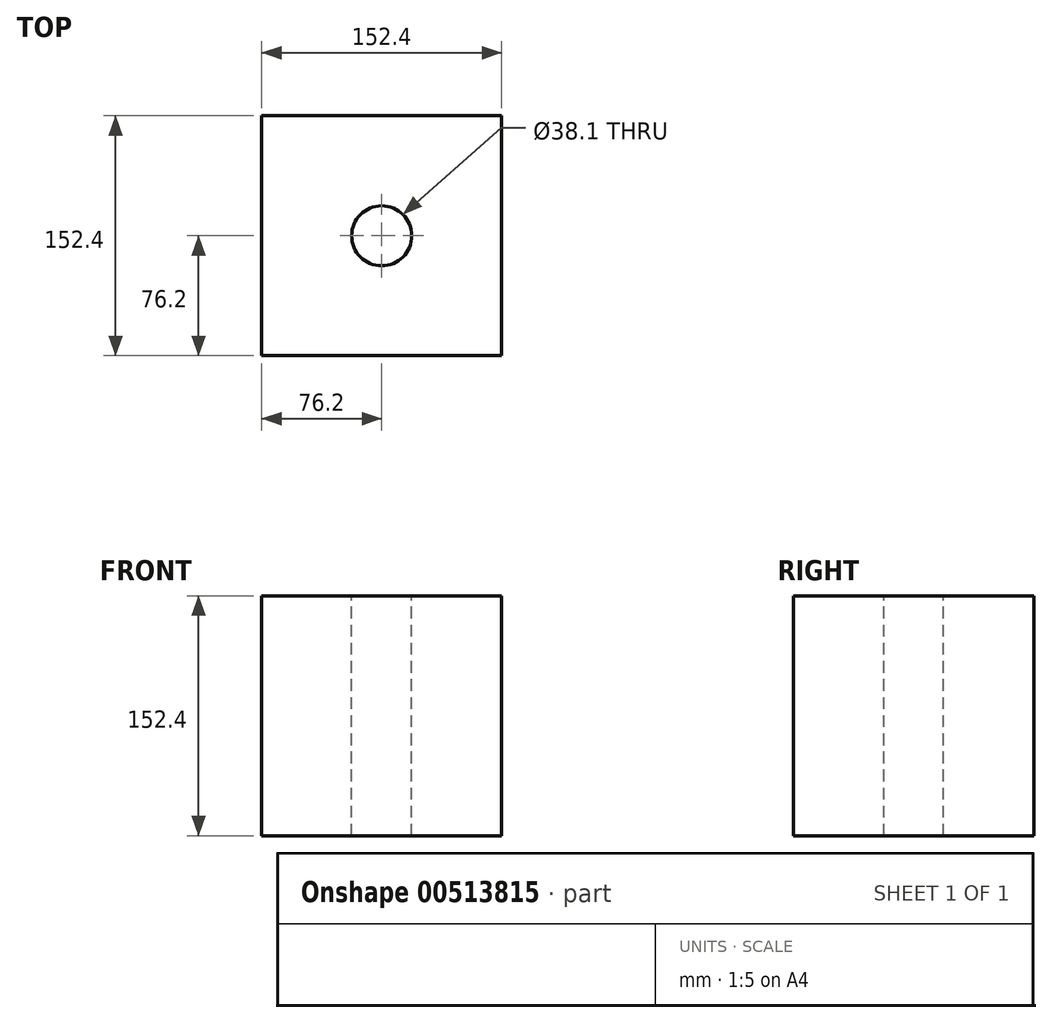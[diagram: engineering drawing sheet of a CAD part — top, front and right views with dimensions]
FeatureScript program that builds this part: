
annotation { "Feature Type Name" : "Feature", "Feature Type Description" : "" }
export const myFeature = defineFeature(function(context is Context, id is Id, definition is map)
    precondition{}
    {
        {
            var Q0;
            Q0=qCreatedBy(makeId("Top.planeOp"),FACE);
            var sketch = newSketch(context, id + "F0", { "sketchPlane" : qUnion([Q0])});
            skLineSegment(sketch, "E0.bottom", {"start": v(76.2, -76.2) * mm, "end": v(-76.2, -76.2) * mm});
            skLineSegment(sketch, "E0.top", {"start": v(76.2, 76.2) * mm, "end": v(-76.2, 76.2) * mm});
            skLineSegment(sketch, "E0.left", {"start": v(76.2, -76.2) * mm, "end": v(76.2, 76.2) * mm});
            skLineSegment(sketch, "E0.right", {"start": v(-76.2, -76.2) * mm, "end": v(-76.2, 76.2) * mm});
            skPoint(sketch, "E0.middle", {"position": v(0, 0) * mm});
            skCircle(sketch, "E1", {"center": v(0, 0) * mm, "radius": 19.05 * mm});
            skSolve(sketch);
        }
        {
            var Q0;
            Q0=makeQuery(id+"F0.imprint","IMPRINT",FACE,{"disambiguationData":[TD([[makeQuery(id+"F0.imprint","IMPRINT",EDGE,{"derivedFrom":sQuery(id+"F0.wireOp",EDGE,"E0.bottom")}),-1.0]])]});
            extrude(context, id + "F1", {"entities" : qUnion([Q0]), "oppositeDirection" : true, "depth" : 152.4 * mm});
        }
    });
